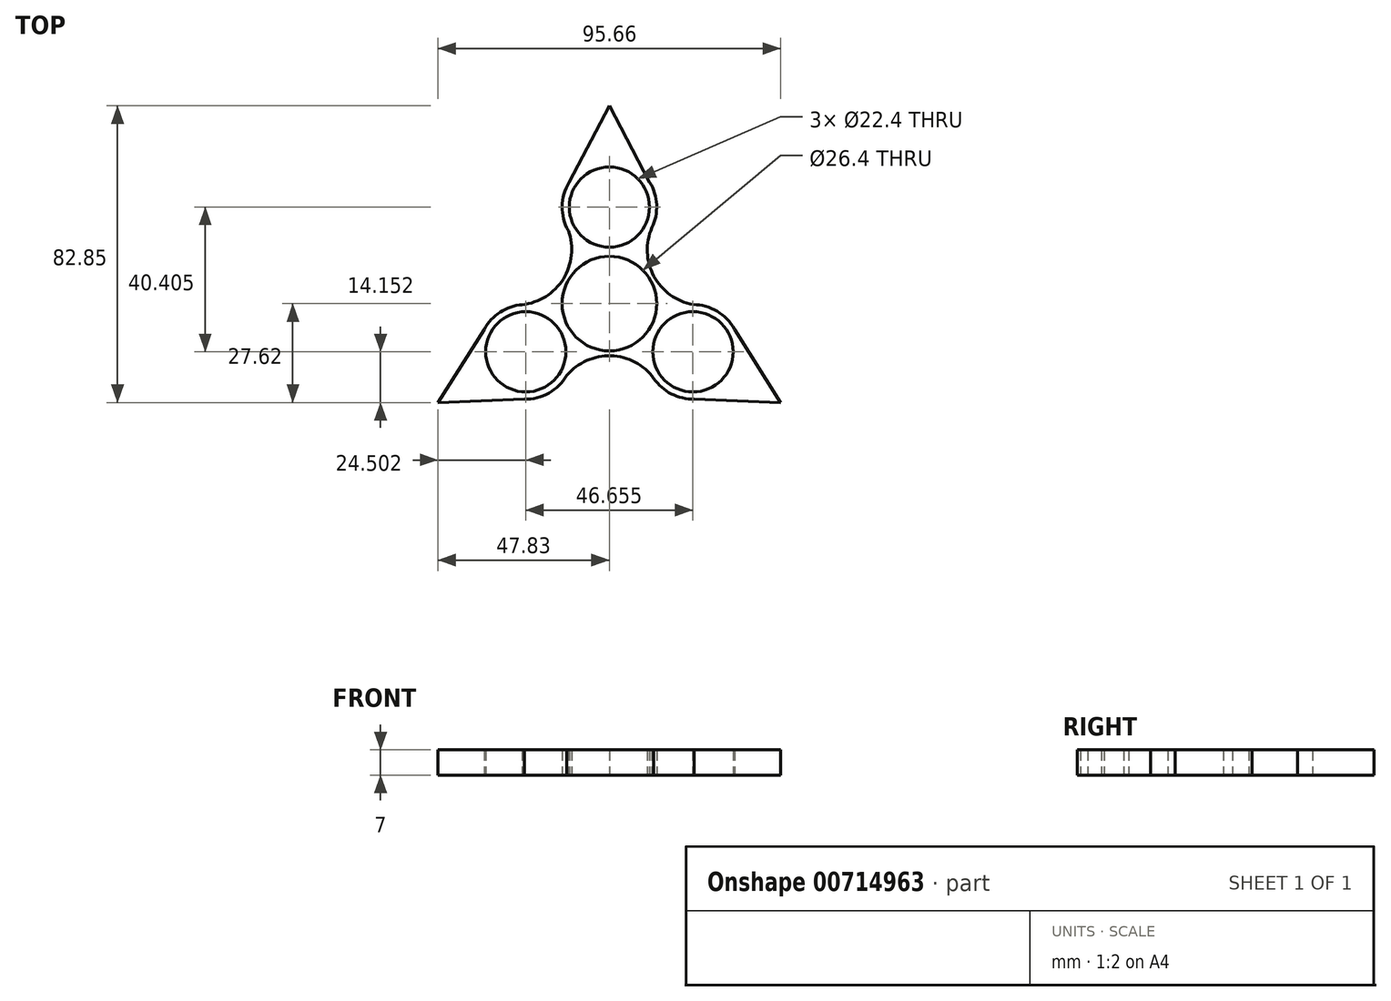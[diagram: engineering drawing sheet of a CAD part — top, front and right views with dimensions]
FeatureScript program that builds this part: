
annotation { "Feature Type Name" : "Feature", "Feature Type Description" : "" }
export const myFeature = defineFeature(function(context is Context, id is Id, definition is map)
    precondition{}
    {
        {
            var Q0;
            Q0=qCreatedBy(makeId("Top.planeOp"),FACE);
            var sketch = newSketch(context, id + "F0", { "sketchPlane" : qUnion([Q0])});
            skCircle(sketch, "E0", {"center": v(0, 0) * mm, "radius": 11.2 * mm});
            skCircle(sketch, "E1", {"center": v(0, 0) * mm, "radius": 13.2 * mm});
            skCircle(sketch, "E2", {"center": v(0, 26.94) * mm, "radius": 11.2 * mm});
            skArc(sketch, "E3", {"start": v(11.88, 21.2) * mm, "mid": v(-0.48, 40.13) * mm, "end": v(-11.43, 20.34) * mm});
            skArc(sketch, "E4.1.0", {"start": v(-24.3, -0.3) * mm, "mid": v(-34.51, -20.48) * mm, "end": v(-11.9, -20.07) * mm});
            skCircle(sketch, "E4.1.1", {"center": v(-23.33, -13.47) * mm, "radius": 11.2 * mm});
            skArc(sketch, "E4.2.0", {"start": v(12.4, -20.89) * mm, "mid": v(35, -19.65) * mm, "end": v(23.33, -0.27) * mm});
            skCircle(sketch, "E4.2.1", {"center": v(23.33, -13.47) * mm, "radius": 11.2 * mm});
            skLineSegment(sketch, "E5", {"start": v(-12.06, 32.3) * mm, "end": v(0, 55.23) * mm});
            skLineSegment(sketch, "E6", {"start": v(0, 55.23) * mm, "end": v(12.06, 32.3) * mm});
            skLineSegment(sketch, "E7.1.0", {"start": v(-47.83, -27.62) * mm, "end": v(-34, -5.7) * mm});
            skLineSegment(sketch, "E7.1.1", {"start": v(-21.94, -26.6) * mm, "end": v(-47.83, -27.62) * mm});
            skLineSegment(sketch, "E7.2.0", {"start": v(47.83, -27.62) * mm, "end": v(21.94, -26.6) * mm});
            skLineSegment(sketch, "E7.2.1", {"start": v(34, -5.7) * mm, "end": v(47.83, -27.62) * mm});
            skArc(sketch, "E8", {"start": v(12.1, 21.66) * mm, "mid": v(12.28, 7.91) * mm, "end": v(23.33, -0.27) * mm});
            skArc(sketch, "E9.1.0", {"start": v(-24.81, -0.35) * mm, "mid": v(-13, 6.68) * mm, "end": v(-11.43, 20.34) * mm});
            skArc(sketch, "E9.2.0", {"start": v(12.71, -21.31) * mm, "mid": v(0.72, -14.59) * mm, "end": v(-11.9, -20.07) * mm});
            skSolve(sketch);
        }
        {
            var Q0;
            Q0 = qSketchRegion(id + "F0", true);
            extrude(context, id + "F1", {"entities" : qUnion([Q0]), "depth" : 7 * mm, "offsetDistance" : 25 * mm});
        }
    });
